# Revit family: Plumbing-Flushometer-Sloan-Valve-Sloan-186-SFSM_
name_source: partatom
category: Plumbing Fixtures
units: mm (PartAtom-declared; Revit-internal decimal feet)

## family parameters
Cut with Voids When Loaded = No
Host = Face
OmniClass Number = 23.45.05.14.99
OmniClass Title = Other Sanitary Washing Plumbing Fixtures
Part Type = Normal
Room Calculation Point = No
Round Connector Dimension = Use Diameter
Shared = No

## types (11) — shared parameters
Apparent Load = 0 VA
Assembly Code = D2020300
CW Connection = Yes
Centerline of Supply from Top of Fixture = 11 1/2"
Centerline of Supply to Centerline of Valve = 4 3/4"
Current = 0 A
Default Elevation = 0"
Edition number = 1
HW Connection = No
Height = 13 1/2"
Keynote = 15410
Manufacturer = Sloan Valve
Number of Poles = 1
Operating Water Pressure = 15 – 80 PSI (103 – 552 kPa)
Power Factor = 1
Product Material = Sloan Valve - Finish - Polished Chrome
Product data url = https://bimobject.com
URL = www.sloanvalve.com
Valve Pressure Drop = 0.00 psi
Vent Connection = No
Waste Connection = No
Water Inlet Connection Diameter = 1"
zero-valued in all types: CWFU, HWFU, WFU

## per-type parameters (varying)
| type | Description | Flush Rate | Hardwired | Number | Part Number | Voltage |
| SLOAN 186 SFSM-0.25-HW | 0.25 gpf, Polished Chrome Finish, Fixture Connection Top Spud, Single Flush, Hardwired, Sloan® Exposed Sensor Urinal Flushometer. | 0.25 gpf (0.9 Lpf) | Yes | 3 | 3782694 | 6 V |
| SLOAN 186 SFSM-0.25 | 0.25 gpf, Polished Chrome Finish, Fixture Connection Top Spud, Single Flush, Battery, Sloan® Exposed Sensor Urinal Flushometer. | 0.25 gpf (0.9 Lpf) | No | 2 | 3782687 | 0 V |
| SLOAN 186 SFSM-0.5-HW | 0.5 gpf, Polished Chrome Finish, Fixture Connection Top Spud, Single Flush, Hardwired, Sloan® Exposed Sensor Urinal Flushometer. | 0.5 gpf (1.9 Lpf) | Yes | 3 | 3782693 | 6 V |
| SLOAN 186 SFSM-1.0-YBC-DFB | 1.0 gpf, Cast Set Screw Wall Flange, Dual-Filtered Fixed Bypass Diaphragm, Polished Chrome Finish, Fixture Connection Top Spud, Single Flush, Battery, Sloan® Exposed Sensor Urinal Flushometer. | 1.0 gpf (3.8 Lpf) | No | 2 | 37826002 | 0 V |
| SLOAN 186 SFSM-1.0-DFB | 1.0 gpf, Dual-Filtered Fixed Bypass Diaphragm, Polished Chrome Finish, Fixture Connection Top Spud, Single Flush, Battery, Sloan® Exposed Sensor Urinal Flushometer. | 1.0 gpf (3.8 Lpf) | No | 2 | 3782690 | 0 V |
| SLOAN 186 SFSM-0.125-HW | 0.125 gpf, Polished Chrome Finish, Fixture Connection Top Spud, Single Flush, Hardwired, Sloan® Exposed Sensor Urinal Flushometer | 0.125 gpf (0.5 Lpf) | Yes | 3 | 3782695 | 6 V |
| SLOAN 186 SFSM-1.0-HW | 1.0 gpf, Polished Chrome Finish, Fixture Connection Top Spud, Single Flush, Hardwired, Sloan® Exposed Sensor Urinal Flushometer. | 1.0 gpf (3.8 Lpf) | Yes | 3 | 3782692 | 6 V |
| SLOAN 186 SFSM-0.5-DFB | 0.5 gpf, Dual-Filtered Fixed Bypass Diaphragm, Polished Chrome Finish, Fixture Connection Top Spud, Single Flush, Battery, Sloan® Exposed Sensor Urinal Flushometer. | 0.5 gpf (1.9 Lpf) | No | 2 | 3782691 | 0 V |
| SLOAN 186 SFSM-0.5 | 0.5 gpf, Polished Chrome Finish, Fixture Connection Top Spud, Single Flush, Battery, Sloan® Exposed Sensor Urinal Flushometer. | 0.5 gpf (1.9 Lpf) | No | 2 | 3782686 | 0 V |
| SLOAN 186 SFSM-1.0 | 1.0 gpf, Polished Chrome Finish, Fixture Connection Top Spud, Single Flush, Battery, Sloan® Exposed Sensor Urinal Flushometer. | 1.0 gpf (3.8 Lpf) | No | 2 | 3782685 | 0 V |
| SLOAN 186 SFSM-0.125 | 0.125 gpf, Polished Chrome Finish, Fixture Connection Top Spud, Single Flush, Battery, Sloan® Exposed Sensor Urinal Flushometer. | 0.125 gpf (0.5 Lpf) | No | 2 | 3782688 | 0 V |

note: column(s) folded — value = type name in every type: Model

## geometry (parser evidence)
native form markers: Sweep x7
no freeform markers — native parametric forms only
